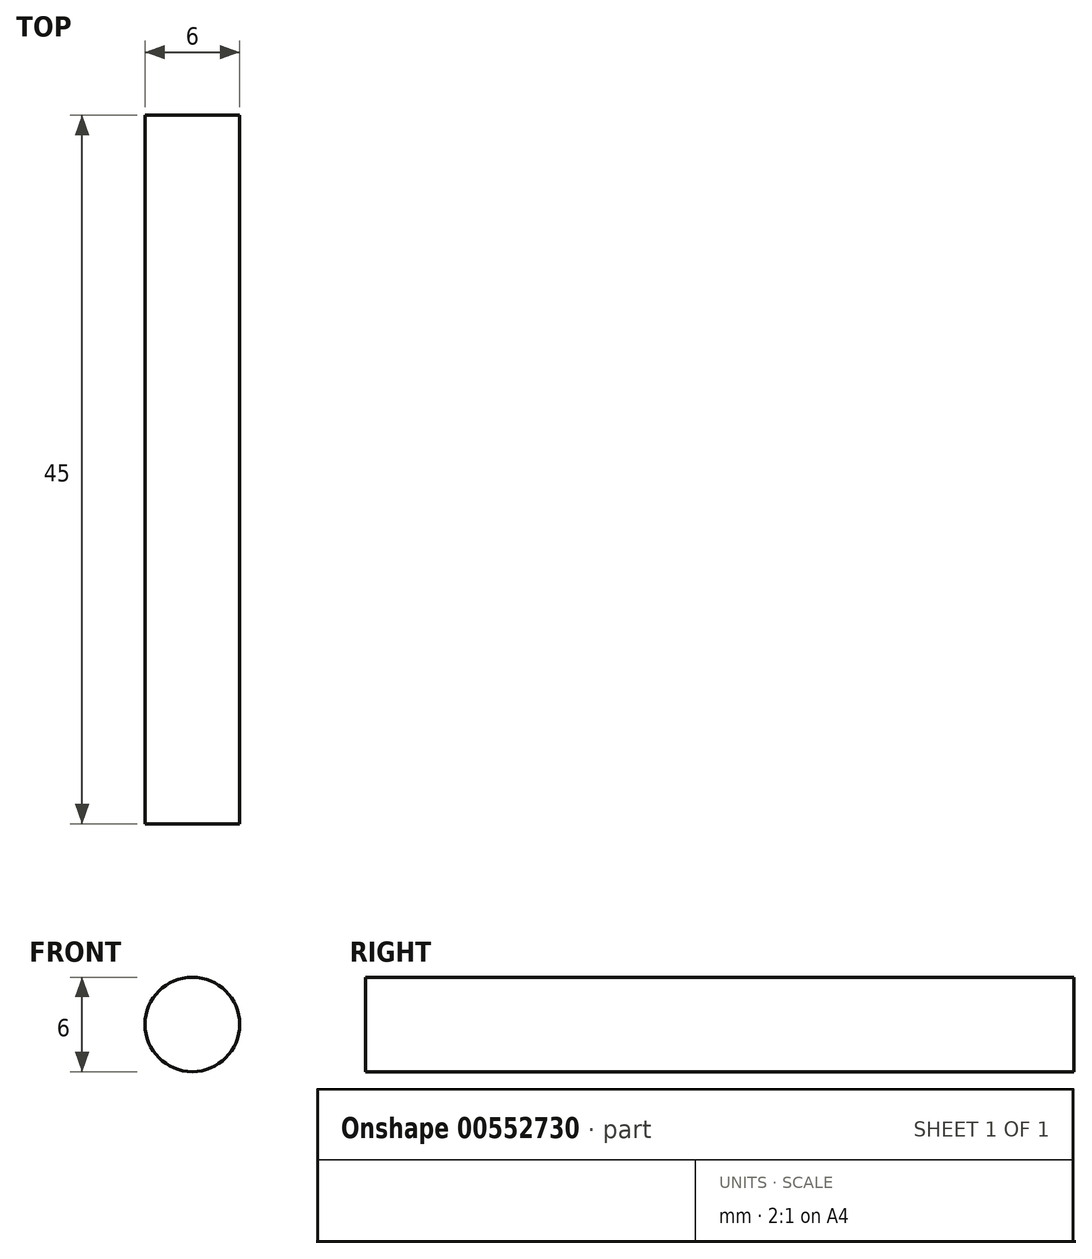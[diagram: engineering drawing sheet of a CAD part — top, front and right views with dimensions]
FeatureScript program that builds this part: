
annotation { "Feature Type Name" : "Feature", "Feature Type Description" : "" }
export const myFeature = defineFeature(function(context is Context, id is Id, definition is map)
    precondition{}
    {
        {
            var Q0;
            Q0=qCreatedBy(makeId("Front.planeOp"),FACE);
            var sketch = newSketch(context, id + "F0", { "sketchPlane" : qUnion([Q0])});
            skCircle(sketch, "E0", {"center": v(0, 0) * mm, "radius": 3 * mm});
            skSolve(sketch);
        }
        {
            var Q0;
            Q0=makeQuery(id+"F0.imprint","IMPRINT",FACE,{"disambiguationData":[TD([[makeQuery(id+"F0.imprint","IMPRINT",EDGE,{"derivedFrom":sQuery(id+"F0.wireOp",EDGE,"E0")}),1.0]])]});
            extrude(context, id + "F1", {"entities" : qUnion([Q0]), "depth" : 45 * mm, "offsetDistance" : 25 * mm});
        }
    });
